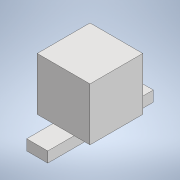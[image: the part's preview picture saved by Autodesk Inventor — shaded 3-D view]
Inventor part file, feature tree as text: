
AUTODESK INVENTOR PART (.ipt)
format: ipt  version: 2022 (Build 260153000, 153)  size: 110,080 bytes
history: native  units: mm
features: extrude x3, sketch x3
ambient origin geometry x8: Origin, YZ Plane, XZ Plane, XY Plane, X Axis, Y Axis, Z Axis, Center Point
bodies: Solid1 (feature_tree)
feature tree (6):
  extrude  "Extrusion1"  Depth=100.0mm
  extrude  "Extrusion2"  Depth=50.0mm
  extrude  "Extrusion3"  Depth=30.0mm TaperAngle=0.0deg
  sketch  "Sketch1"  dims[d0=20.0mm d1=100.0mm]
  sketch  "Sketch2"  dims[d2=10.0mm d3=0.0mm d4=50.0mm]
  sketch  "Sketch3"  dims[d5=50.0mm d6=30.0mm d7=0.0mm d8=20.0mm d9=0.0mm d10=0.0mm]
